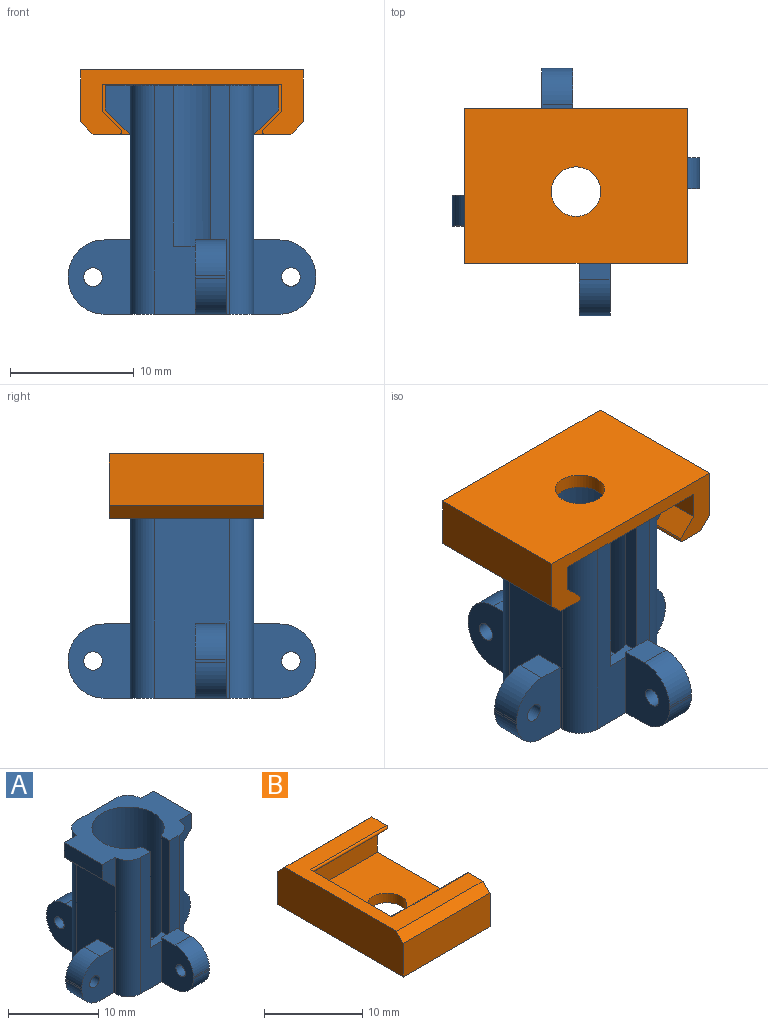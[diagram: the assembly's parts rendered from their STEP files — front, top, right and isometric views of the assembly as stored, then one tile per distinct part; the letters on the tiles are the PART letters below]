
ASSEMBLY  parts=2 mates=1
PART A: 54 faces, bbox 20x20x18.5 mm
  f0: plane 14.5x6mm, normal (-1,0,0), area 72mm2, adj f8,f9,f10,f11,f25,f26,f52
  f1: plane 18.5x3.25mm, normal (0,-1,0), area 37.4mm2, adj f2,f8,f21,f26,f38,f40
  f2: plane 14x10mm, normal (0,0,1), area 67mm2, adj f1,f3,f6,f7,f25,f26,f27,f28
  f3: cylinder r=4mm len=17mm, axis (0,0,1), area 387.3mm2, adj f2,f37,f38,f39,f40
  f4: cylinder r=2.25mm len=4.5mm, axis (0,0,-1), area 21.2mm2, adj f8,f37
  f5: plane 14.5x6mm, normal (1,0,0), area 72mm2, adj f8,f17,f18,f19,f27,f28,f53
  f6: plane 18.5x6mm, normal (0,1,0), area 96mm2, adj f2,f8,f13,f14,f15,f25,f28
  f7: plane 18.5x1.5mm, normal (0,-1,0), area 20.2mm2, adj f2,f8,f22,f23,f27,f39
  f8: plane 14.21x14.21mm, normal (0,0,-1), area 101.7mm2, adj f0,f1,f4,f5,f6,f7,f9,f10
  f9: plane 6x5mm, normal (0,1,0), area 24.6mm2, adj f0,f8,f11,f12,f35,f36,f43
  f10: plane 6x5mm, normal (0,-1,0), area 24.6mm2, adj f0,f8,f11,f12,f35,f36,f43
  f11: plane 2.5x2.1mm, normal (0,0,1), area 5.3mm2, adj f0,f9,f10,f36
  f12: plane 2.5x0.21mm, normal (-1,0,0), area 0.5mm2, adj f9,f10,f35,f36
  f13: plane 6x5mm, normal (1,0,0), area 24.6mm2, adj f6,f8,f15,f16,f33,f34,f44
  f14: plane 6x5mm, normal (-1,0,0), area 24.6mm2, adj f6,f8,f15,f16,f33,f34,f44
  f15: plane 2.5x2.1mm, normal (0,0,1), area 5.3mm2, adj f6,f13,f14,f34
  f16: plane 2.5x0.21mm, normal (0,1,0), area 0.5mm2, adj f13,f14,f33,f34
  f17: plane 6x5mm, normal (0,-1,0), area 24.6mm2, adj f5,f8,f19,f20,f31,f32,f45
  f18: plane 6x5mm, normal (0,1,0), area 24.6mm2, adj f5,f8,f19,f20,f31,f32,f45
  f19: plane 2.5x2.1mm, normal (0,0,1), area 5.3mm2, adj f5,f17,f18,f32
  f20: plane 2.5x0.21mm, normal (1,0,0), area 0.5mm2, adj f17,f18,f31,f32
  f21: plane 6x5mm, normal (-1,0,0), area 24.6mm2, adj f1,f8,f23,f24,f29,f30,f41,f42
  f22: plane 6x5mm, normal (1,0,0), area 24.6mm2, adj f7,f8,f23,f24,f29,f30,f42
  f23: plane 2.5x2.1mm, normal (0,0,1), area 5.3mm2, adj f7,f21,f22,f30,f41
  f24: plane 2.5x0.21mm, normal (0,-1,0), area 0.5mm2, adj f21,f22,f29,f30
  f25: cylinder r=2mm len=18.5mm, axis (0,0,1), area 58.1mm2, adj f0,f2,f6,f8,f46
  f26: cylinder r=2mm len=18.5mm, axis (0,0,-1), area 58.1mm2, adj f0,f1,f2,f8,f47
  f27: cylinder r=2mm len=18.5mm, axis (0,0,1), area 58.1mm2, adj f2,f5,f7,f8,f49
  f28: cylinder r=2mm len=18.5mm, axis (0,0,-1), area 58.1mm2, adj f2,f5,f6,f8,f50
  f29: cylinder r=2.9mm len=2.9mm, axis (-1,0,0), area 11.4mm2, adj f8,f21,f22,f24
  f30: cylinder r=2.9mm len=2.9mm, axis (1,0,0), area 11.4mm2, adj f21,f22,f23,f24
  f31: cylinder r=2.9mm len=2.9mm, axis (0,1,0), area 11.4mm2, adj f8,f17,f18,f20
  f32: cylinder r=2.9mm len=2.9mm, axis (0,1,0), area 11.4mm2, adj f17,f18,f19,f20
  f33: cylinder r=2.9mm len=2.9mm, axis (-1,0,0), area 11.4mm2, adj f8,f13,f14,f16
  f34: cylinder r=2.9mm len=2.9mm, axis (-1,0,0), area 11.4mm2, adj f13,f14,f15,f16
  f35: cylinder r=2.9mm len=2.9mm, axis (0,1,0), area 11.4mm2, adj f8,f9,f10,f12
  f36: cylinder r=2.9mm len=2.9mm, axis (0,-1,0), area 11.4mm2, adj f9,f10,f11,f12
  f37: plane 8x8mm, normal (0,0,1), area 34.4mm2, adj f3,f4
  f38: plane 13x1.29mm, normal (1,0,0), area 16.8mm2, adj f1,f2,f3,f40
  f39: plane 13x1.29mm, normal (-1,0,0), area 16.8mm2, adj f2,f3,f7,f40,f41
  f40: plane 3x1.29mm, normal (0,0,1), area 3.3mm2, adj f1,f3,f38,f39,f41
  f41: plane 1.25x0.5mm, normal (0,1,0), area 0.6mm2, adj f21,f23,f39,f40
  f42: cylinder r=0.75mm len=2.5mm, axis (1,0,0), area 11.8mm2, adj f21,f22
  f43: cylinder r=0.75mm len=2.5mm, axis (0,-1,0), area 11.8mm2, adj f9,f10
  f44: cylinder r=0.75mm len=2.5mm, axis (-1,0,0), area 11.8mm2, adj f13,f14
  f45: cylinder r=0.75mm len=2.5mm, axis (0,1,0), area 11.8mm2, adj f17,f18
  f46: plane 4x2mm, normal (0,1,0), area 6mm2, adj f2,f25,f48,f52
  f47: plane 4x2mm, normal (0,-1,0), area 6mm2, adj f2,f26,f48,f52
  f48: plane 6x2mm, normal (-1,0,0), area 12mm2, adj f2,f46,f47,f52
  f49: plane 4x2mm, normal (0,-1,0), area 6mm2, adj f2,f27,f51,f53
  f50: plane 4x2mm, normal (0,1,0), area 6mm2, adj f2,f28,f51,f53
  f51: plane 6x2mm, normal (1,0,0), area 12mm2, adj f2,f49,f50,f53
  f52: plane 6x2mm, normal (-0.71,0,-0.71), area 17mm2, adj f0,f46,f47,f48
  f53: plane 6x2mm, normal (0.71,0,-0.71), area 17mm2, adj f5,f49,f50,f51
PART B: 17 faces, bbox 12.5x18x5.2 mm
  f0: plane 14.4x11mm, normal (0,0,1), area 145.8mm2, adj f3,f5,f6,f10,f16
  f1: plane 12.5x4.2mm, normal (0,1,0), area 52.5mm2, adj f3,f4,f13,f15
  f2: plane 12.5x4.2mm, normal (0,-1,0), area 52.5mm2, adj f3,f4,f14,f15
  f3: plane 18x5.2mm, normal (1,0,0), area 38.1mm2, adj f0,f1,f2,f4,f6,f7,f8,f9
  f4: plane 18x12.5mm, normal (0,0,-1), area 212.4mm2, adj f1,f2,f3,f5,f15
  f5: cylinder r=2mm len=4mm, axis (0,0,1), area 15.1mm2, adj f0,f4
  f6: plane 11x2.2mm, normal (0,-1,0), area 24.2mm2, adj f0,f3,f7,f16
  f7: plane 11x1.46mm, normal (0,-0.71,-0.71), area 22.7mm2, adj f3,f6,f12,f16
  f8: plane 16x12.5mm, normal (0,0,1), area 70.6mm2, adj f3,f11,f12,f13,f14,f15,f16
  f9: plane 11x1.46mm, normal (0,0.71,-0.71), area 22.7mm2, adj f3,f10,f11,f16
  f10: plane 11x2.2mm, normal (0,1,0), area 24.2mm2, adj f0,f3,f9,f16
  f11: cylinder r=0.2mm len=11mm, axis (-1,0,0), area 5.2mm2, adj f3,f8,f9,f16
  f12: cylinder r=0.2mm len=11mm, axis (-1,0,0), area 5.2mm2, adj f3,f7,f8,f16
  f13: plane 12.5x1mm, normal (0,0.71,0.71), area 17.7mm2, adj f1,f3,f8,f15
  f14: plane 12.5x1mm, normal (0,-0.71,0.71), area 17.7mm2, adj f2,f3,f8,f15
  f15: plane 18x5.2mm, normal (-1,0,0), area 92.6mm2, adj f1,f2,f4,f8,f13,f14
  f16: plane 14.4x4mm, normal (1,0,0), area 54.5mm2, adj f0,f6,f7,f8,f9,f10,f11,f12
PLACE A t=(0.66,0.09,0.66)mm fixed
PLACE B rot(axis=(-0.71,0.71,0),180deg) t=(0.66,-0.21,20.41)mm
MATE slider B.f5 <-> A.f3  axis (0,0,1) through (0.66,0.09,20.41)mm
